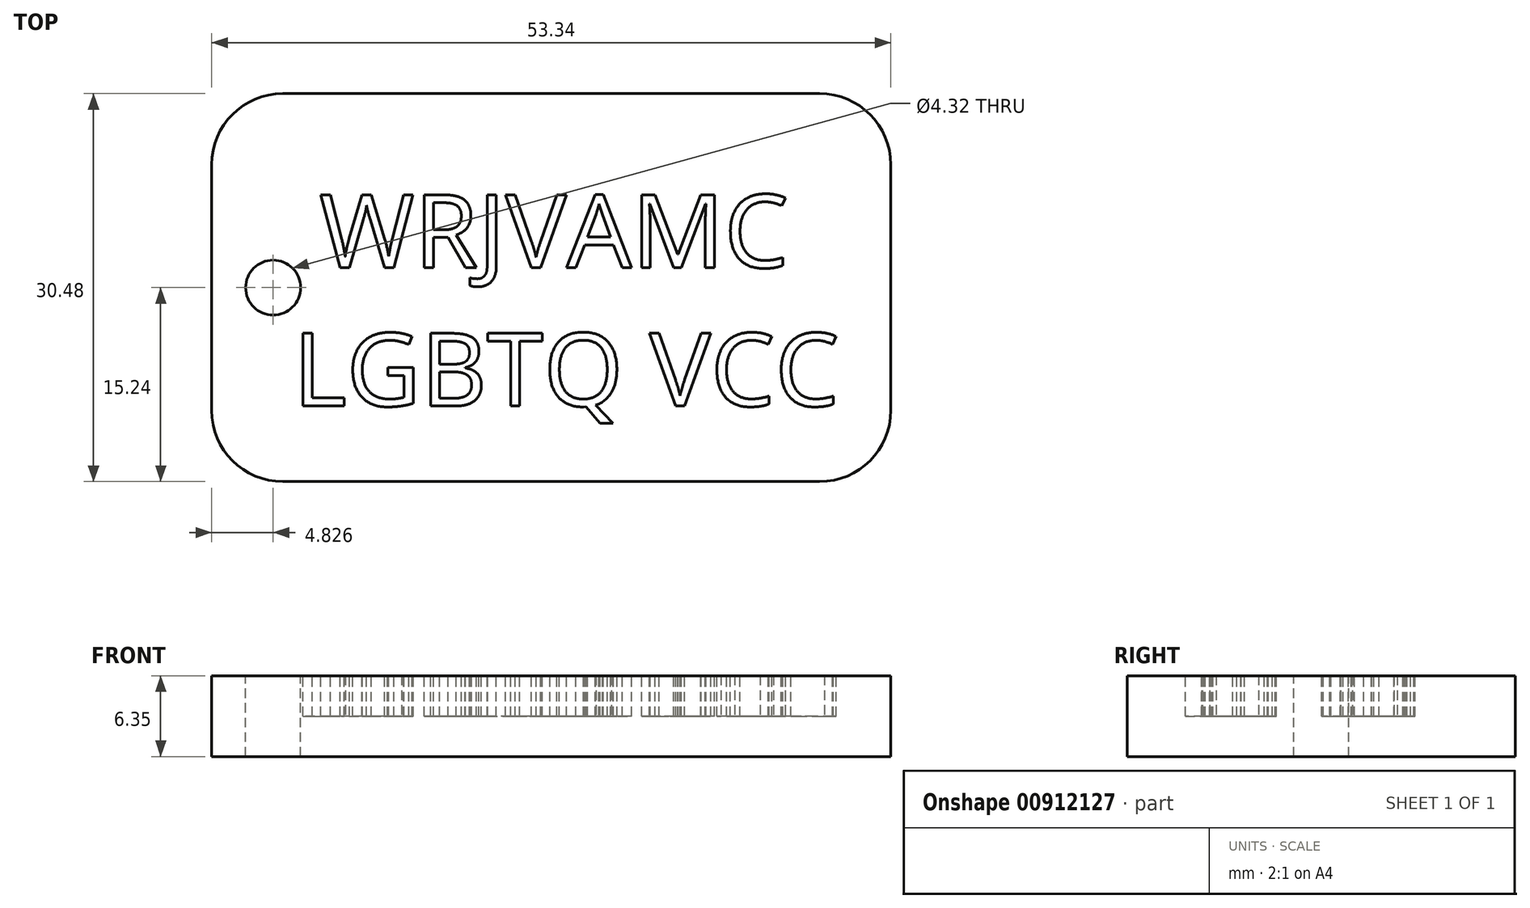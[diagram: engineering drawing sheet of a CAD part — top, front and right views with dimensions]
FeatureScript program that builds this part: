
annotation { "Feature Type Name" : "Feature", "Feature Type Description" : "" }
export const myFeature = defineFeature(function(context is Context, id is Id, definition is map)
    precondition{}
    {
        {
            var Q0;
            Q0=qCreatedBy(makeId("Top.planeOp"),FACE);
            var sketch = newSketch(context, id + "F0", { "sketchPlane" : qUnion([Q0])});
            skLineSegment(sketch, "E0.bottom", {"start": v(5.59, 0) * mm, "end": v(47.75, 0) * mm});
            skLineSegment(sketch, "E0.top", {"start": v(5.59, -30.48) * mm, "end": v(47.75, -30.48) * mm});
            skLineSegment(sketch, "E0.left", {"start": v(0, -5.59) * mm, "end": v(0, -24.9) * mm});
            skLineSegment(sketch, "E0.right", {"start": v(53.34, -5.59) * mm, "end": v(53.34, -24.9) * mm});
            skPoint(sketch, "E1.visualSharp", {"position": v(0, 0) * mm});
            skArc(sketch, "E1.filletArc", {"start": v(5.59, 0) * mm, "mid": v(1.64, -1.64) * mm, "end": v(0, -5.59) * mm});
            skPoint(sketch, "E2.visualSharp", {"position": v(0, -30.48) * mm});
            skArc(sketch, "E2.filletArc", {"start": v(0, -24.9) * mm, "mid": v(1.64, -28.84) * mm, "end": v(5.59, -30.48) * mm});
            skPoint(sketch, "E3.visualSharp", {"position": v(53.34, -30.48) * mm});
            skArc(sketch, "E3.filletArc", {"start": v(47.75, -30.48) * mm, "mid": v(51.7, -28.84) * mm, "end": v(53.34, -24.9) * mm});
            skPoint(sketch, "E4.visualSharp", {"position": v(53.34, 0) * mm});
            skArc(sketch, "E4.filletArc", {"start": v(53.34, -5.59) * mm, "mid": v(51.7, -1.64) * mm, "end": v(47.75, 0) * mm});
            skSolve(sketch);
        }
        {
            var Q0;
            Q0=makeQuery(id+"F0.imprint","IMPRINT",FACE,{"disambiguationData":[TD([[makeQuery(id+"F0.imprint","IMPRINT",EDGE,{"derivedFrom":sQuery(id+"F0.wireOp",EDGE,"E0.bottom")}),-1.0]])]});
            var Q1;
            Q1=sQuery(id+"F0.wireOp",EDGE,"E1.filletArc");
            var Q2;
            Q2=sQuery(id+"F0.wireOp",EDGE,"E0.bottom");
            var Q3;
            Q3=sQuery(id+"F0.wireOp",EDGE,"E4.filletArc");
            var Q4;
            Q4=sQuery(id+"F0.wireOp",EDGE,"E0.right");
            var Q5;
            Q5=sQuery(id+"F0.wireOp",EDGE,"E3.filletArc");
            var Q6;
            Q6=sQuery(id+"F0.wireOp",EDGE,"E0.top");
            var Q7;
            Q7=sQuery(id+"F0.wireOp",EDGE,"E2.filletArc");
            var Q8;
            Q8=sQuery(id+"F0.wireOp",EDGE,"E0.left");
            extrude(context, id + "F1", {"entities" : qUnion([Q0]), "surfaceEntities" : qUnion([Q1, Q2, Q3, Q4, Q5, Q6, Q7, Q8]), "oppositeDirection" : true, "depth" : 6.35 * mm, "offsetDistance" : 25.4 * mm});
        }
        {
            var Q0;
            Q0=qCreatedBy(makeId("Top.planeOp"),FACE);
            var sketch = newSketch(context, id + "F2", { "sketchPlane" : qUnion([Q0])});
            skText(sketch, "E5", { "text": " WRJVAMC\nLGBTQ VCC", "fontName": "NotoSans-Regular.ttf"});
            skCircle(sketch, "E6", {"center": v(4.83, -15.24) * mm, "radius": 2.16 * mm});
            skLineSegment(sketch, "E7.0", {"start": v(5.59, 0) * mm, "end": v(47.75, 0) * mm});
            skLineSegment(sketch, "E7.1", {"start": v(5.59, -30.48) * mm, "end": v(47.75, -30.48) * mm});
            skLineSegment(sketch, "E7.2", {"start": v(0, -5.59) * mm, "end": v(0, -24.9) * mm});
            skLineSegment(sketch, "E7.3", {"start": v(53.34, -5.59) * mm, "end": v(53.34, -24.9) * mm});
            skPoint(sketch, "E7.4", {"position": v(0, 0) * mm});
            skArc(sketch, "E7.5", {"start": v(5.59, 0) * mm, "mid": v(1.64, -1.64) * mm, "end": v(0, -5.59) * mm});
            skPoint(sketch, "E7.6", {"position": v(0, -30.48) * mm});
            skArc(sketch, "E7.7", {"start": v(0, -24.9) * mm, "mid": v(1.64, -28.84) * mm, "end": v(5.59, -30.48) * mm});
            skPoint(sketch, "E7.8", {"position": v(53.34, -30.48) * mm});
            skArc(sketch, "E7.9", {"start": v(47.75, -30.48) * mm, "mid": v(51.7, -28.84) * mm, "end": v(53.34, -24.9) * mm});
            skPoint(sketch, "E7.10", {"position": v(53.34, 0) * mm});
            skArc(sketch, "E7.11", {"start": v(53.34, -5.59) * mm, "mid": v(51.7, -1.64) * mm, "end": v(47.75, 0) * mm});
            skLineSegment(sketch, "E8", {"start": v(15.35, 0) * mm, "end": v(-11.15, 0) * mm, "construction": true});
            skLineSegment(sketch, "E9", {"start": v(15.35, -30.48) * mm, "end": v(-10.98, -30.48) * mm, "construction": true});
            skLineSegment(sketch, "E10", {"start": v(4.83, 0) * mm, "end": v(4.83, -30.48) * mm, "construction": true});
            const initialGuessF2  = {"E5": [0.0064, -0.01366, 1, 0, 0.00576]};
            skSetInitialGuess(sketch, initialGuessF2);
            skSolve(sketch);
        }
        {
            var Q0;
            Q0=makeQuery(id+"F2.imprint","IMPRINT",FACE,{"disambiguationData":[TD([[makeQuery(id+"F2.imprint","IMPRINT",EDGE,{"derivedFrom":sQuery(id+"F2.wireOp",EDGE,"E5.sketch_text.stroke-103")}),-1.0]])]});
            var Q1;
            Q1=makeQuery(id+"F2.imprint","IMPRINT",FACE,{"disambiguationData":[TD([[makeQuery(id+"F2.imprint","IMPRINT",EDGE,{"derivedFrom":sQuery(id+"F2.wireOp",EDGE,"E5.sketch_text.stroke-109")}),-1.0]])]});
            var Q2;
            Q2=makeQuery(id+"F2.imprint","IMPRINT",FACE,{"disambiguationData":[TD([[makeQuery(id+"F2.imprint","IMPRINT",EDGE,{"derivedFrom":sQuery(id+"F2.wireOp",EDGE,"E5.sketch_text.stroke-129")}),-1.0]])]});
            var Q3;
            Q3=makeQuery(id+"F2.imprint","IMPRINT",FACE,{"disambiguationData":[TD([[makeQuery(id+"F2.imprint","IMPRINT",EDGE,{"derivedFrom":sQuery(id+"F2.wireOp",EDGE,"E5.sketch_text.stroke-155")}),-1.0]])]});
            var Q4;
            Q4=makeQuery(id+"F2.imprint","IMPRINT",FACE,{"disambiguationData":[TD([[makeQuery(id+"F2.imprint","IMPRINT",EDGE,{"derivedFrom":sQuery(id+"F2.wireOp",EDGE,"E5.sketch_text.stroke-163")}),-1.0]])]});
            var Q5;
            Q5=makeQuery(id+"F2.imprint","IMPRINT",FACE,{"disambiguationData":[TD([[makeQuery(id+"F2.imprint","IMPRINT",EDGE,{"derivedFrom":sQuery(id+"F2.wireOp",EDGE,"E5.sketch_text.stroke-183")}),-1.0]])]});
            var Q6;
            Q6=makeQuery(id+"F2.imprint","IMPRINT",FACE,{"disambiguationData":[TD([[makeQuery(id+"F2.imprint","IMPRINT",EDGE,{"derivedFrom":sQuery(id+"F2.wireOp",EDGE,"E5.sketch_text.stroke-192")}),-1.0]])]});
            var Q7;
            Q7=makeQuery(id+"F2.imprint","IMPRINT",FACE,{"disambiguationData":[TD([[makeQuery(id+"F2.imprint","IMPRINT",EDGE,{"derivedFrom":sQuery(id+"F2.wireOp",EDGE,"E5.sketch_text.stroke-208")}),-1.0]])]});
            var Q8;
            Q8=makeQuery(id+"F2.imprint","IMPRINT",FACE,{"disambiguationData":[TD([[makeQuery(id+"F2.imprint","IMPRINT",EDGE,{"derivedFrom":sQuery(id+"F2.wireOp",EDGE,"E5.sketch_text.stroke-87")}),-1.0]])]});
            var Q9;
            Q9=makeQuery(id+"F2.imprint","IMPRINT",FACE,{"disambiguationData":[TD([[makeQuery(id+"F2.imprint","IMPRINT",EDGE,{"derivedFrom":sQuery(id+"F2.wireOp",EDGE,"E5.sketch_text.stroke-69")}),-1.0]])]});
            var Q10;
            Q10=makeQuery(id+"F2.imprint","IMPRINT",FACE,{"disambiguationData":[TD([[makeQuery(id+"F2.imprint","IMPRINT",EDGE,{"derivedFrom":sQuery(id+"F2.wireOp",EDGE,"E5.sketch_text.stroke-56")}),-1.0]])]});
            var Q11;
            Q11=makeQuery(id+"F2.imprint","IMPRINT",FACE,{"disambiguationData":[TD([[makeQuery(id+"F2.imprint","IMPRINT",EDGE,{"derivedFrom":sQuery(id+"F2.wireOp",EDGE,"E5.sketch_text.stroke-47")}),-1.0]])]});
            var Q12;
            Q12=makeQuery(id+"F2.imprint","IMPRINT",FACE,{"disambiguationData":[TD([[makeQuery(id+"F2.imprint","IMPRINT",EDGE,{"derivedFrom":sQuery(id+"F2.wireOp",EDGE,"E5.sketch_text.stroke-37")}),-1.0]])]});
            var Q13;
            Q13=makeQuery(id+"F2.imprint","IMPRINT",FACE,{"disambiguationData":[TD([[makeQuery(id+"F2.imprint","IMPRINT",EDGE,{"derivedFrom":sQuery(id+"F2.wireOp",EDGE,"E5.sketch_text.stroke-19")}),-1.0]])]});
            var Q14;
            Q14=makeQuery(id+"F2.imprint","IMPRINT",FACE,{"disambiguationData":[TD([[makeQuery(id+"F2.imprint","IMPRINT",EDGE,{"derivedFrom":sQuery(id+"F2.wireOp",EDGE,"E5.sketch_text.stroke-0")}),-1.0]])]});
            extrude(context, id + "F3", {"entities" : qUnion([Q0, Q1, Q2, Q3, Q4, Q5, Q6, Q7, Q8, Q9, Q10, Q11, Q12, Q13, Q14]), "operationType" : NewBodyOperationType.REMOVE, "oppositeDirection" : true, "depth" : 3.17 * mm, "offsetDistance" : 25.4 * mm});
        }
        {
            var Q0;
            Q0=makeQuery(id+"F2.imprint","IMPRINT",FACE,{"disambiguationData":[TD([[makeQuery(id+"F2.imprint","IMPRINT",EDGE,{"derivedFrom":sQuery(id+"F2.wireOp",EDGE,"E6")}),1.0]])]});
            extrude(context, id + "F4", {"entities" : qUnion([Q0]), "operationType" : NewBodyOperationType.REMOVE, "oppositeDirection" : true, "depth" : 25.4 * mm, "offsetDistance" : 25.4 * mm});
        }
    });
